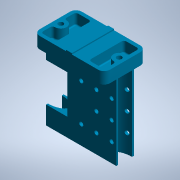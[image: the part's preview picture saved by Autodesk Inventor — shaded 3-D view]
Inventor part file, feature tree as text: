
AUTODESK INVENTOR PART (.ipt)
format: ipt  version: 2020 (Build 240168000, 168)  size: 408,064 bytes
history: native  units: mm
features: sketch x8, extrude x6, fillet x5, hole x2, mirror x2
ambient origin geometry x8: Origin, YZ Plane, XZ Plane, XY Plane, X Axis, Y Axis, Z Axis, Center Point
bodies: Solid1 (feature_tree)
feature tree (23):
  extrude  "Extrusion1"  Depth=36.0mm
  hole  "Hole1"  [1 undecoded]
  fillet  "Fillet1"  Radius=1.0mm
  extrude  "Extrusion3"  Depth=10.0mm TaperAngle=0.0deg
  fillet  "Fillet2"  Radius=5.0mm
  fillet  "Fillet3"  Radius=3.0mm
  fillet  "Fillet4"  Radius=3.0mm
  fillet  "Fillet5"  Radius=5.0mm
  mirror  "Mirror3"
  mirror  "Mirror2"
  extrude  "Extrusion2"  Depth=15.5mm
  extrude  "Extrusion4"  Depth=15.5mm TaperAngle=0.0deg
  extrude  "Extrusion5"  Depth=15.5mm
  hole  "Perçage3"  [1 undecoded]
  extrude  "Extrusion6"  Depth=5.0mm
  sketch  "Sketch1"  dims[d0=36.0mm d1=30.0mm]
  sketch  "Sketch2"  dims[d3=10.0mm d4=0.0mm d5=25.0mm]
  sketch  "Sketch4"  dims[d6=4.2mm d7=6.0mm d8=4.0mm d9=2.0mm d10=90.0deg d11=8.0mm d12=20.594885mm d22=1.0mm]
  sketch  "Sketch5"  dims[d23=5.0mm d24=10.0mm d25=0.0mm d26=5.0mm d27=3.0mm d28=3.0mm d29=5.0mm]
  sketch  "Sketch6"  dims[d30=14.0mm d31=6.0mm d32=9.0mm d33=0.0mm d34=2.0mm d35=2.0mm d36=5.0mm d37=1.0mm d38=64.0mm d40=15.0mm d42=10.5mm d44=60.0mm d45=0.0mm d47=10.0mm d48=0.0mm d58=12.0mm d59=6.0mm d62=16.0mm d63=13.0mm d65=17.0mm d66=16.0mm d67=13.0mm d68=3.5mm d69=6.0mm d70=4.0mm d71=2.0mm d72=90.0deg d73=8.0mm d74=20.594885mm d76=64.0mm d82=33.0mm d83=18.0mm d85=0.0mm d86=0.0mm d87=32.0mm d88=15.5mm]
  sketch  "Esquisse10"
  sketch  "Esquisse11"
  sketch  "Esquisse13"
note: 2 required parameter values undecoded (feature->parameter linkage not recoverable at this tier; creation-order binding heuristic only, values carry confidence <= 0.55)
